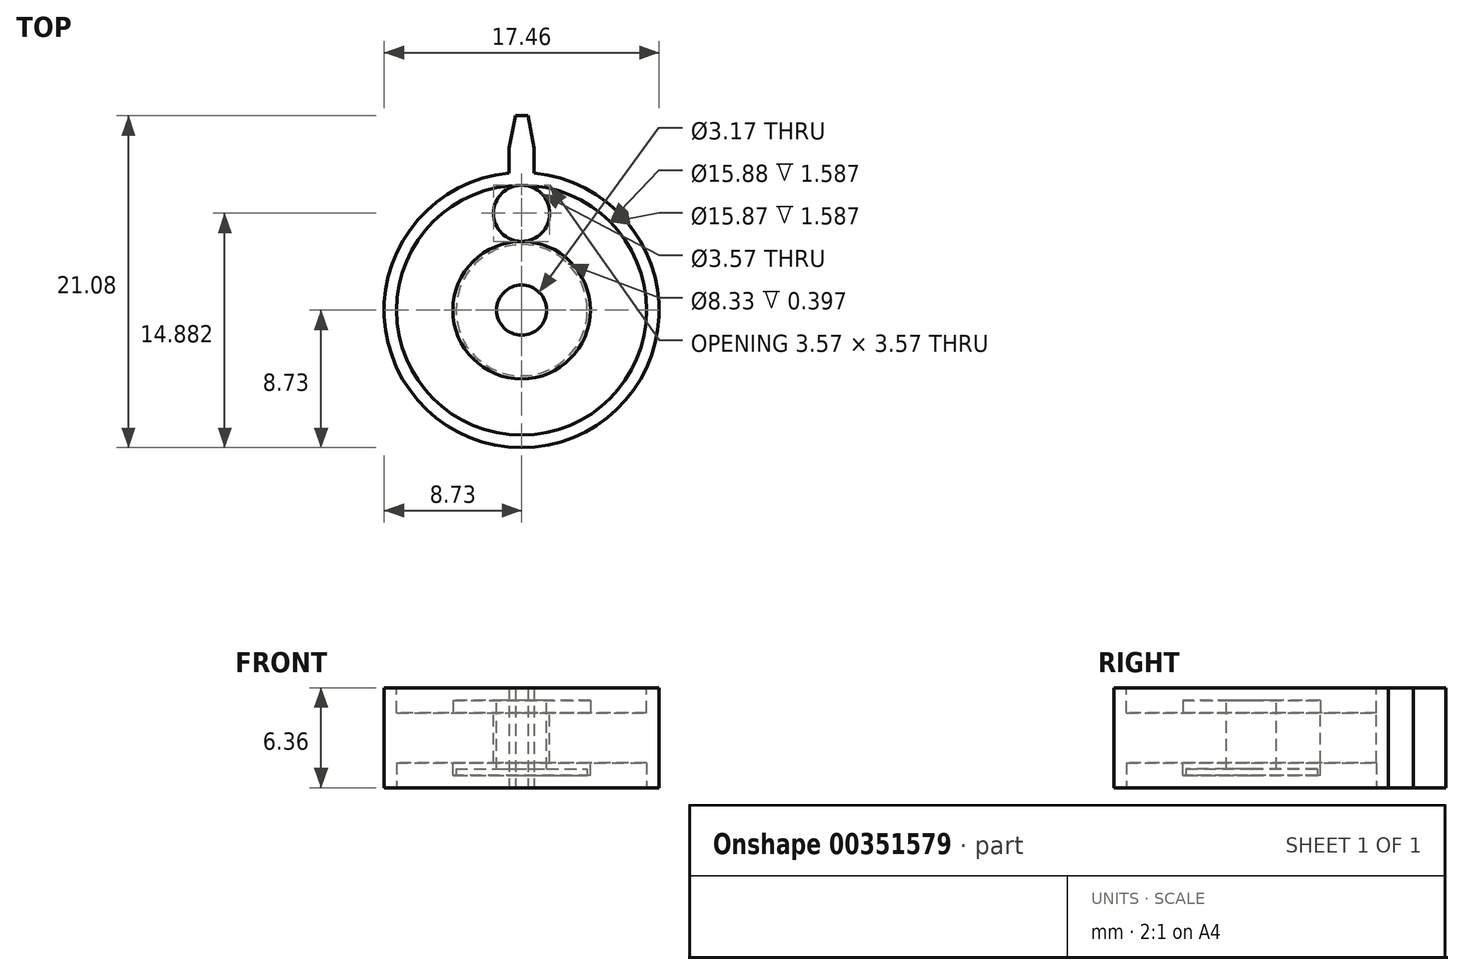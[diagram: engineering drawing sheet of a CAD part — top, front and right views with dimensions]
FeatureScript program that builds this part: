
annotation { "Feature Type Name" : "Feature", "Feature Type Description" : "" }
export const myFeature = defineFeature(function(context is Context, id is Id, definition is map)
    precondition{}
    {
        {
            var Q0;
            Q0=qCreatedBy(makeId("Top.planeOp"),FACE);
            var sketch = newSketch(context, id + "F0", { "sketchPlane" : qUnion([Q0])});
            skCircle(sketch, "E0", {"center": v(0, 0) * mm, "radius": 8.73 * mm});
            skSolve(sketch);
        }
        {
            var Q0;
            Q0 = qSketchRegion(id + "F0", true);
            extrude(context, id + "F1", {"entities" : qUnion([Q0]), "depth" : 6.35 * mm, "symmetric" : true});
        }
        {
            var Q0;
            Q0=qCreatedBy(makeId("Top.planeOp"),FACE);
            var sketch = newSketch(context, id + "F2", { "sketchPlane" : qUnion([Q0])});
            skArc(sketch, "E1.0", {"start": v(0.8, 8.7) * mm, "mid": v(0, 8.73) * mm, "end": v(-0.8, 8.7) * mm});
            skLineSegment(sketch, "E2.bottom", {"start": v(-0.8, 8.7) * mm, "end": v(0.8, 8.7) * mm});
            skLineSegment(sketch, "E2.left", {"start": v(-0.8, 8.7) * mm, "end": v(-0.8, 10.28) * mm});
            skLineSegment(sketch, "E2.right", {"start": v(0.8, 8.7) * mm, "end": v(0.8, 10.28) * mm});
            skLineSegment(sketch, "E3", {"start": v(-0.8, 10.28) * mm, "end": v(-0.4, 12.35) * mm});
            skLineSegment(sketch, "E4", {"start": v(-0.4, 12.35) * mm, "end": v(0.4, 12.35) * mm});
            skLineSegment(sketch, "E5", {"start": v(0.4, 12.35) * mm, "end": v(0.8, 10.28) * mm});
            skLineSegment(sketch, "E6", {"start": v(0, 12.34) * mm, "end": v(0, 11.25) * mm, "construction": true});
            skSolve(sketch);
        }
        {
            var Q0;
            Q0 = qSketchRegion(id + "F2", true);
            var Q1;
            Q1=makeQuery(id+"F1.opExtrude","CAP_FACE",FACE,{"disambiguationData":[OSD([sQuery(id+"F0.wireOp",EDGE,"E0")])],"isStart":false});
            var Q2;
            Q2=makeQuery(id+"F1.opExtrude","CAP_FACE",FACE,{"disambiguationData":[OSD([sQuery(id+"F0.wireOp",EDGE,"E0")])],"isStart":true});
            extrude(context, id + "F3", {"entities" : qUnion([Q0]), "operationType" : NewBodyOperationType.ADD, "endBound" : BoundingType.UP_TO_SURFACE, "endBoundEntityFace" : qUnion([Q1]), "depth" : 25.4 * mm, "hasSecondDirection" : true, "secondDirectionBound" : BoundingType.UP_TO_SURFACE, "secondDirectionOppositeDirection" : true, "secondDirectionBoundEntityFace" : qUnion([Q2]), "secondDirectionDepth" : 25.4 * mm});
        }
        {
            var Q0;
            {var subQ0=sQuery(id+"F0.wireOp",EDGE,"E0");Q0=makeQuery(id+"FdBI0uL5yzSovcb_1.19.F3.boolean.opBoolean","MERGE",FACE,{"derivedFrom":[makeQuery(id+"FdBI0uL5yzSovcb_1.18.F3.boolean.opBoolean","MERGE",FACE,{"derivedFrom":[makeQuery(id+"FdBI0uL5yzSovcb_1.17.F3.boolean.opBoolean","MERGE",FACE,{"derivedFrom":[makeQuery(id+"FdBI0uL5yzSovcb_1.16.F3.boolean.opBoolean","MERGE",FACE,{"derivedFrom":[makeQuery(id+"FdBI0uL5yzSovcb_1.15.F3.boolean.opBoolean","MERGE",FACE,{"derivedFrom":[makeQuery(id+"FdBI0uL5yzSovcb_1.14.F3.boolean.opBoolean","MERGE",FACE,{"derivedFrom":[makeQuery(id+"FdBI0uL5yzSovcb_1.13.F3.boolean.opBoolean","MERGE",FACE,{"derivedFrom":[makeQuery(id+"FdBI0uL5yzSovcb_1.12.F3.boolean.opBoolean","MERGE",FACE,{"derivedFrom":[makeQuery(id+"FdBI0uL5yzSovcb_1.11.F3.boolean.opBoolean","MERGE",FACE,{"derivedFrom":[makeQuery(id+"FdBI0uL5yzSovcb_1.10.F3.boolean.opBoolean","MERGE",FACE,{"derivedFrom":[makeQuery(id+"FdBI0uL5yzSovcb_1.9.F3.boolean.opBoolean","MERGE",FACE,{"derivedFrom":[makeQuery(id+"FdBI0uL5yzSovcb_1.8.F3.boolean.opBoolean","MERGE",FACE,{"derivedFrom":[makeQuery(id+"FdBI0uL5yzSovcb_1.7.F3.boolean.opBoolean","MERGE",FACE,{"derivedFrom":[makeQuery(id+"FdBI0uL5yzSovcb_1.6.F3.boolean.opBoolean","MERGE",FACE,{"derivedFrom":[makeQuery(id+"FdBI0uL5yzSovcb_1.5.F3.boolean.opBoolean","MERGE",FACE,{"derivedFrom":[makeQuery(id+"FdBI0uL5yzSovcb_1.4.F3.boolean.opBoolean","MERGE",FACE,{"derivedFrom":[makeQuery(id+"FdBI0uL5yzSovcb_1.3.F3.boolean.opBoolean","MERGE",FACE,{"derivedFrom":[makeQuery(id+"FdBI0uL5yzSovcb_1.2.F3.boolean.opBoolean","MERGE",FACE,{"derivedFrom":[makeQuery(id+"FdBI0uL5yzSovcb_1.1.F3.boolean.opBoolean","MERGE",FACE,{"derivedFrom":[makeQuery(id+"F3.boolean.opBoolean","MERGE",FACE,{"derivedFrom":[makeQuery(id+"F1.opExtrude","CAP_FACE",FACE,{"disambiguationData":[OSD([subQ0])],"isStart":false}),makeQuery(id+"F3.opExtrude","CAP_FACE",FACE,{"disambiguationData":[OSD([subQ0])],"isStart":false})]}),makeQuery(id+"FdBI0uL5yzSovcb_1.1.F3.opExtrude","CAP_FACE",FACE,{"disambiguationData":[OSD([subQ0])],"isStart":false})]}),makeQuery(id+"FdBI0uL5yzSovcb_1.2.F3.opExtrude","CAP_FACE",FACE,{"disambiguationData":[OSD([subQ0])],"isStart":false})]}),makeQuery(id+"FdBI0uL5yzSovcb_1.3.F3.opExtrude","CAP_FACE",FACE,{"disambiguationData":[OSD([subQ0])],"isStart":false})]}),makeQuery(id+"FdBI0uL5yzSovcb_1.4.F3.opExtrude","CAP_FACE",FACE,{"disambiguationData":[OSD([subQ0])],"isStart":false})]}),makeQuery(id+"FdBI0uL5yzSovcb_1.5.F3.opExtrude","CAP_FACE",FACE,{"disambiguationData":[OSD([subQ0])],"isStart":false})]}),makeQuery(id+"FdBI0uL5yzSovcb_1.6.F3.opExtrude","CAP_FACE",FACE,{"disambiguationData":[OSD([subQ0])],"isStart":false})]}),makeQuery(id+"FdBI0uL5yzSovcb_1.7.F3.opExtrude","CAP_FACE",FACE,{"disambiguationData":[OSD([subQ0])],"isStart":false})]}),makeQuery(id+"FdBI0uL5yzSovcb_1.8.F3.opExtrude","CAP_FACE",FACE,{"disambiguationData":[OSD([subQ0])],"isStart":false})]}),makeQuery(id+"FdBI0uL5yzSovcb_1.9.F3.opExtrude","CAP_FACE",FACE,{"disambiguationData":[OSD([subQ0])],"isStart":false})]}),makeQuery(id+"FdBI0uL5yzSovcb_1.10.F3.opExtrude","CAP_FACE",FACE,{"disambiguationData":[OSD([subQ0])],"isStart":false})]}),makeQuery(id+"FdBI0uL5yzSovcb_1.11.F3.opExtrude","CAP_FACE",FACE,{"disambiguationData":[OSD([subQ0])],"isStart":false})]}),makeQuery(id+"FdBI0uL5yzSovcb_1.12.F3.opExtrude","CAP_FACE",FACE,{"disambiguationData":[OSD([subQ0])],"isStart":false})]}),makeQuery(id+"FdBI0uL5yzSovcb_1.13.F3.opExtrude","CAP_FACE",FACE,{"disambiguationData":[OSD([subQ0])],"isStart":false})]}),makeQuery(id+"FdBI0uL5yzSovcb_1.14.F3.opExtrude","CAP_FACE",FACE,{"disambiguationData":[OSD([subQ0])],"isStart":false})]}),makeQuery(id+"FdBI0uL5yzSovcb_1.15.F3.opExtrude","CAP_FACE",FACE,{"disambiguationData":[OSD([subQ0])],"isStart":false})]}),makeQuery(id+"FdBI0uL5yzSovcb_1.16.F3.opExtrude","CAP_FACE",FACE,{"disambiguationData":[OSD([subQ0])],"isStart":false})]}),makeQuery(id+"FdBI0uL5yzSovcb_1.17.F3.opExtrude","CAP_FACE",FACE,{"disambiguationData":[OSD([subQ0])],"isStart":false})]}),makeQuery(id+"FdBI0uL5yzSovcb_1.18.F3.opExtrude","CAP_FACE",FACE,{"disambiguationData":[OSD([subQ0])],"isStart":false})]}),makeQuery(id+"FdBI0uL5yzSovcb_1.19.F3.opExtrude","CAP_FACE",FACE,{"disambiguationData":[OSD([subQ0])],"isStart":false})]});}
            var sketch = newSketch(context, id + "F4", { "sketchPlane" : qUnion([Q0])});
            skCircle(sketch, "E7", {"center": v(0, 0) * mm, "radius": 7.94 * mm});
            skSolve(sketch);
        }
        {
            var Q0;
            Q0 = qSketchRegion(id + "F4", true);
            extrude(context, id + "F5", {"entities" : qUnion([Q0]), "operationType" : NewBodyOperationType.REMOVE, "oppositeDirection" : true, "depth" : 1.59 * mm});
        }
        {
            var Q0;
            {var subQ0=sQuery(id+"F0.wireOp",EDGE,"E0");Q0=makeQuery(id+"FdBI0uL5yzSovcb_1.19.F3.boolean.opBoolean","MERGE",FACE,{"derivedFrom":[makeQuery(id+"FdBI0uL5yzSovcb_1.18.F3.boolean.opBoolean","MERGE",FACE,{"derivedFrom":[makeQuery(id+"FdBI0uL5yzSovcb_1.17.F3.boolean.opBoolean","MERGE",FACE,{"derivedFrom":[makeQuery(id+"FdBI0uL5yzSovcb_1.16.F3.boolean.opBoolean","MERGE",FACE,{"derivedFrom":[makeQuery(id+"FdBI0uL5yzSovcb_1.15.F3.boolean.opBoolean","MERGE",FACE,{"derivedFrom":[makeQuery(id+"FdBI0uL5yzSovcb_1.14.F3.boolean.opBoolean","MERGE",FACE,{"derivedFrom":[makeQuery(id+"FdBI0uL5yzSovcb_1.13.F3.boolean.opBoolean","MERGE",FACE,{"derivedFrom":[makeQuery(id+"FdBI0uL5yzSovcb_1.12.F3.boolean.opBoolean","MERGE",FACE,{"derivedFrom":[makeQuery(id+"FdBI0uL5yzSovcb_1.11.F3.boolean.opBoolean","MERGE",FACE,{"derivedFrom":[makeQuery(id+"FdBI0uL5yzSovcb_1.10.F3.boolean.opBoolean","MERGE",FACE,{"derivedFrom":[makeQuery(id+"FdBI0uL5yzSovcb_1.9.F3.boolean.opBoolean","MERGE",FACE,{"derivedFrom":[makeQuery(id+"FdBI0uL5yzSovcb_1.8.F3.boolean.opBoolean","MERGE",FACE,{"derivedFrom":[makeQuery(id+"FdBI0uL5yzSovcb_1.7.F3.boolean.opBoolean","MERGE",FACE,{"derivedFrom":[makeQuery(id+"FdBI0uL5yzSovcb_1.6.F3.boolean.opBoolean","MERGE",FACE,{"derivedFrom":[makeQuery(id+"FdBI0uL5yzSovcb_1.5.F3.boolean.opBoolean","MERGE",FACE,{"derivedFrom":[makeQuery(id+"FdBI0uL5yzSovcb_1.4.F3.boolean.opBoolean","MERGE",FACE,{"derivedFrom":[makeQuery(id+"FdBI0uL5yzSovcb_1.3.F3.boolean.opBoolean","MERGE",FACE,{"derivedFrom":[makeQuery(id+"FdBI0uL5yzSovcb_1.2.F3.boolean.opBoolean","MERGE",FACE,{"derivedFrom":[makeQuery(id+"FdBI0uL5yzSovcb_1.1.F3.boolean.opBoolean","MERGE",FACE,{"derivedFrom":[makeQuery(id+"F3.boolean.opBoolean","MERGE",FACE,{"derivedFrom":[makeQuery(id+"F1.opExtrude","CAP_FACE",FACE,{"disambiguationData":[OSD([subQ0])],"isStart":true}),makeQuery(id+"F3.opExtrude","CAP_FACE",FACE,{"disambiguationData":[OSD([subQ0])],"isStart":true})]}),makeQuery(id+"FdBI0uL5yzSovcb_1.1.F3.opExtrude","CAP_FACE",FACE,{"disambiguationData":[OSD([subQ0])],"isStart":true})]}),makeQuery(id+"FdBI0uL5yzSovcb_1.2.F3.opExtrude","CAP_FACE",FACE,{"disambiguationData":[OSD([subQ0])],"isStart":true})]}),makeQuery(id+"FdBI0uL5yzSovcb_1.3.F3.opExtrude","CAP_FACE",FACE,{"disambiguationData":[OSD([subQ0])],"isStart":true})]}),makeQuery(id+"FdBI0uL5yzSovcb_1.4.F3.opExtrude","CAP_FACE",FACE,{"disambiguationData":[OSD([subQ0])],"isStart":true})]}),makeQuery(id+"FdBI0uL5yzSovcb_1.5.F3.opExtrude","CAP_FACE",FACE,{"disambiguationData":[OSD([subQ0])],"isStart":true})]}),makeQuery(id+"FdBI0uL5yzSovcb_1.6.F3.opExtrude","CAP_FACE",FACE,{"disambiguationData":[OSD([subQ0])],"isStart":true})]}),makeQuery(id+"FdBI0uL5yzSovcb_1.7.F3.opExtrude","CAP_FACE",FACE,{"disambiguationData":[OSD([subQ0])],"isStart":true})]}),makeQuery(id+"FdBI0uL5yzSovcb_1.8.F3.opExtrude","CAP_FACE",FACE,{"disambiguationData":[OSD([subQ0])],"isStart":true})]}),makeQuery(id+"FdBI0uL5yzSovcb_1.9.F3.opExtrude","CAP_FACE",FACE,{"disambiguationData":[OSD([subQ0])],"isStart":true})]}),makeQuery(id+"FdBI0uL5yzSovcb_1.10.F3.opExtrude","CAP_FACE",FACE,{"disambiguationData":[OSD([subQ0])],"isStart":true})]}),makeQuery(id+"FdBI0uL5yzSovcb_1.11.F3.opExtrude","CAP_FACE",FACE,{"disambiguationData":[OSD([subQ0])],"isStart":true})]}),makeQuery(id+"FdBI0uL5yzSovcb_1.12.F3.opExtrude","CAP_FACE",FACE,{"disambiguationData":[OSD([subQ0])],"isStart":true})]}),makeQuery(id+"FdBI0uL5yzSovcb_1.13.F3.opExtrude","CAP_FACE",FACE,{"disambiguationData":[OSD([subQ0])],"isStart":true})]}),makeQuery(id+"FdBI0uL5yzSovcb_1.14.F3.opExtrude","CAP_FACE",FACE,{"disambiguationData":[OSD([subQ0])],"isStart":true})]}),makeQuery(id+"FdBI0uL5yzSovcb_1.15.F3.opExtrude","CAP_FACE",FACE,{"disambiguationData":[OSD([subQ0])],"isStart":true})]}),makeQuery(id+"FdBI0uL5yzSovcb_1.16.F3.opExtrude","CAP_FACE",FACE,{"disambiguationData":[OSD([subQ0])],"isStart":true})]}),makeQuery(id+"FdBI0uL5yzSovcb_1.17.F3.opExtrude","CAP_FACE",FACE,{"disambiguationData":[OSD([subQ0])],"isStart":true})]}),makeQuery(id+"FdBI0uL5yzSovcb_1.18.F3.opExtrude","CAP_FACE",FACE,{"disambiguationData":[OSD([subQ0])],"isStart":true})]}),makeQuery(id+"FdBI0uL5yzSovcb_1.19.F3.opExtrude","CAP_FACE",FACE,{"disambiguationData":[OSD([subQ0])],"isStart":true})]});}
            var sketch = newSketch(context, id + "F6", { "sketchPlane" : qUnion([Q0])});
            skCircle(sketch, "E8", {"center": v(0, 0) * mm, "radius": 7.94 * mm});
            skSolve(sketch);
        }
        {
            var Q0;
            Q0 = qSketchRegion(id + "F6", true);
            extrude(context, id + "F7", {"entities" : qUnion([Q0]), "operationType" : NewBodyOperationType.REMOVE, "oppositeDirection" : true, "depth" : 1.59 * mm});
        }
        {
            var Q0;
            Q0=makeQuery(id+"F5.boolean.opBoolean","COPY",FACE,{"derivedFrom":makeQuery(id+"F5.opExtrude","CAP_FACE",FACE,{"disambiguationData":[OSD([sQuery(id+"F4.wireOp",EDGE,"E7")])],"isStart":false})});
            var sketch = newSketch(context, id + "F8", { "sketchPlane" : qUnion([Q0])});
            skCircle(sketch, "E9", {"center": v(0, 0) * mm, "radius": 4.37 * mm});
            skSolve(sketch);
        }
        {
            var Q0;
            Q0 = qSketchRegion(id + "F8", true);
            extrude(context, id + "F9", {"entities" : qUnion([Q0]), "operationType" : NewBodyOperationType.ADD, "depth" : 0.8 * mm});
        }
        {
            var Q0;
            Q0=makeQuery(id+"F7.boolean.opBoolean","COPY",FACE,{"derivedFrom":makeQuery(id+"F7.opExtrude","CAP_FACE",FACE,{"disambiguationData":[OSD([sQuery(id+"F6.wireOp",EDGE,"E8")])],"isStart":false})});
            var sketch = newSketch(context, id + "F10", { "sketchPlane" : qUnion([Q0])});
            skCircle(sketch, "E10", {"center": v(0, 0) * mm, "radius": 4.37 * mm});
            skSolve(sketch);
        }
        {
            var Q0;
            Q0 = qSketchRegion(id + "F10", true);
            extrude(context, id + "F11", {"entities" : qUnion([Q0]), "operationType" : NewBodyOperationType.ADD, "depth" : 0.8 * mm});
        }
        {
            var Q0;
            Q0=makeQuery(id+"F5.boolean.opBoolean","COPY",FACE,{"derivedFrom":makeQuery(id+"F5.opExtrude","CAP_FACE",FACE,{"disambiguationData":[OSD([sQuery(id+"F4.wireOp",EDGE,"E7")])],"isStart":false})});
            var sketch = newSketch(context, id + "F12", { "sketchPlane" : qUnion([Q0])});
            skCircle(sketch, "E11", {"center": v(0, 6.15) * mm, "radius": 1.79 * mm});
            skSolve(sketch);
        }
        {
            var Q0;
            Q0 = qSketchRegion(id + "F12", true);
            extrude(context, id + "F13", {"entities" : qUnion([Q0]), "operationType" : NewBodyOperationType.REMOVE, "endBound" : BoundingType.THROUGH_ALL, "oppositeDirection" : true, "depth" : 25.4 * mm});
        }
        {
            var Q0;
            Q0=makeQuery(id+"F9.opExtrude","CAP_FACE",FACE,{"disambiguationData":[OSD([sQuery(id+"F8.wireOp",EDGE,"E9")])],"isStart":false});
            var sketch = newSketch(context, id + "F14", { "sketchPlane" : qUnion([Q0])});
            skCircle(sketch, "E12", {"center": v(0, 0) * mm, "radius": 1.59 * mm});
            skSolve(sketch);
        }
        {
            var Q0;
            Q0 = qSketchRegion(id + "F14", true);
            extrude(context, id + "F15", {"entities" : qUnion([Q0]), "operationType" : NewBodyOperationType.REMOVE, "endBound" : BoundingType.THROUGH_ALL, "oppositeDirection" : true, "depth" : 25.4 * mm});
        }
        {
            var Q0;
            Q0=makeQuery(id+"F11.opExtrude","CAP_FACE",FACE,{"disambiguationData":[OSD([sQuery(id+"F10.wireOp",EDGE,"E10")])],"isStart":false});
            var sketch = newSketch(context, id + "F16", { "sketchPlane" : qUnion([Q0])});
            skCircle(sketch, "E13", {"center": v(0, 0) * mm, "radius": 4.17 * mm});
            skSolve(sketch);
        }
        {
            var Q0;
            Q0 = qSketchRegion(id + "F16", true);
            extrude(context, id + "F17", {"entities" : qUnion([Q0]), "operationType" : NewBodyOperationType.REMOVE, "oppositeDirection" : true, "depth" : 0.4 * mm});
        }
    });
